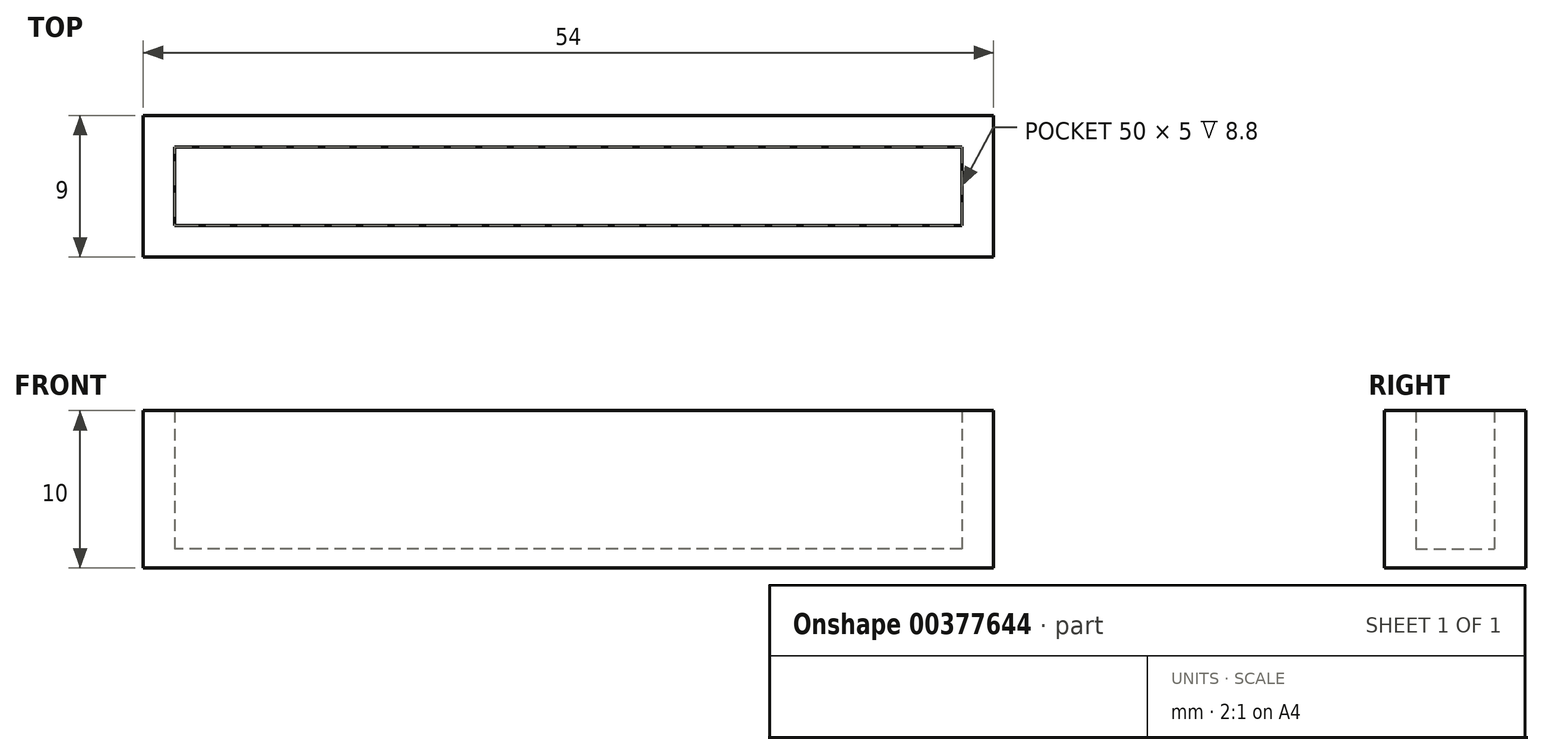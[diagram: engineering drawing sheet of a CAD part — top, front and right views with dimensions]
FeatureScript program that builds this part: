
annotation { "Feature Type Name" : "Feature", "Feature Type Description" : "" }
export const myFeature = defineFeature(function(context is Context, id is Id, definition is map)
    precondition{}
    {
        {
            var Q0;
            Q0=qCreatedBy(makeId("Top.planeOp"),FACE);
            var sketch = newSketch(context, id + "F0", { "sketchPlane" : qUnion([Q0])});
            skLineSegment(sketch, "E0.bottom", {"start": v(-50, 17.1) * mm, "end": v(0, 17.1) * mm});
            skLineSegment(sketch, "E0.top", {"start": v(-50, 12.1) * mm, "end": v(0, 12.1) * mm});
            skLineSegment(sketch, "E0.left", {"start": v(-50, 17.1) * mm, "end": v(-50, 12.1) * mm});
            skLineSegment(sketch, "E0.right", {"start": v(0, 17.1) * mm, "end": v(0, 12.1) * mm});
            skLineSegment(sketch, "E1", {"start": v(-52, 19.1) * mm, "end": v(2, 19.1) * mm});
            skLineSegment(sketch, "E2", {"start": v(2, 19.1) * mm, "end": v(2, 10.1) * mm});
            skLineSegment(sketch, "E3", {"start": v(2, 10.1) * mm, "end": v(-52, 10.1) * mm});
            skLineSegment(sketch, "E4", {"start": v(-52, 19.1) * mm, "end": v(-52, 10.1) * mm});
            skSolve(sketch);
        }
        {
            var Q0;
            Q0=makeQuery(id+"F0.imprint","IMPRINT",FACE,{"disambiguationData":[TD([[makeQuery(id+"F0.imprint","IMPRINT",EDGE,{"derivedFrom":sQuery(id+"F0.wireOp",EDGE,"E0.bottom")}),1.0]])]});
            var Q1;
            Q1=makeQuery(id+"F0.imprint","IMPRINT",FACE,{"disambiguationData":[TD([[makeQuery(id+"F0.imprint","IMPRINT",EDGE,{"derivedFrom":sQuery(id+"F0.wireOp",EDGE,"E0.bottom")}),-1.0]])]});
            extrude(context, id + "F1", {"entities" : qUnion([Q0, Q1]), "depth" : 1.2 * mm});
        }
        {
            var Q0;
            Q0=makeQuery(id+"F0.imprint","IMPRINT",FACE,{"disambiguationData":[TD([[makeQuery(id+"F0.imprint","IMPRINT",EDGE,{"derivedFrom":sQuery(id+"F0.wireOp",EDGE,"E0.bottom")}),1.0]])]});
            extrude(context, id + "F2", {"entities" : qUnion([Q0]), "operationType" : NewBodyOperationType.ADD, "depth" : 10 * mm});
        }
    });
